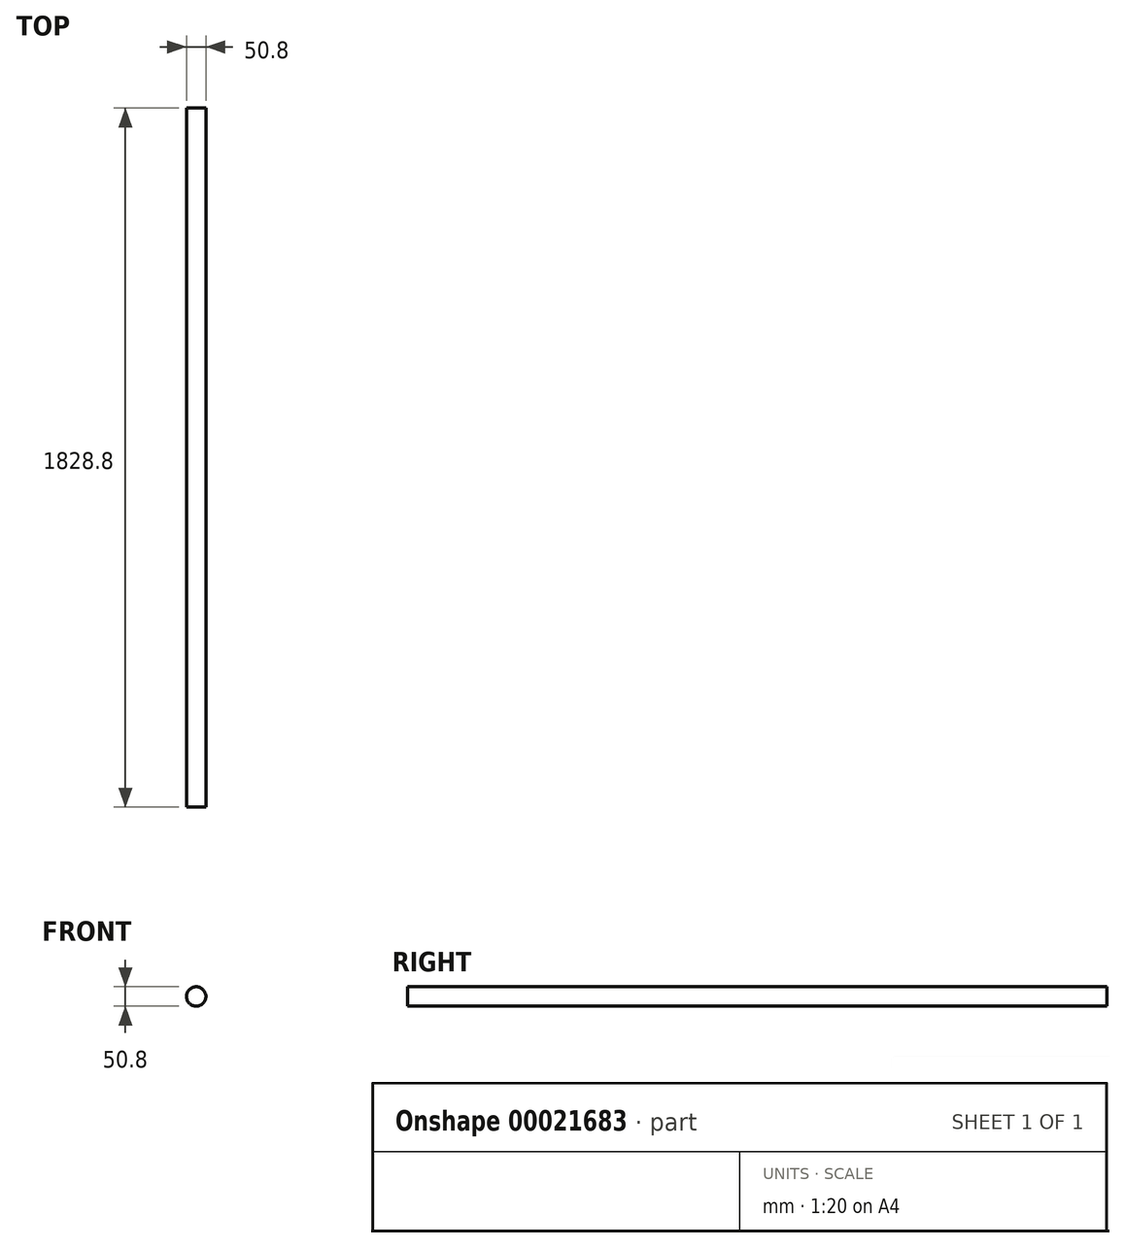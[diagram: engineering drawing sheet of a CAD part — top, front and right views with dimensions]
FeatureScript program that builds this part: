
annotation { "Feature Type Name" : "Feature", "Feature Type Description" : "" }
export const myFeature = defineFeature(function(context is Context, id is Id, definition is map)
    precondition{}
    {
        {
            var Q0;
            Q0=qCreatedBy(makeId("Front.planeOp"),FACE);
            var sketch = newSketch(context, id + "F0", { "sketchPlane" : qUnion([Q0])});
            skCircle(sketch, "E0", {"center": v(-43.74, 5.4) * mm, "radius": 25.4 * mm});
            skSolve(sketch);
        }
        {
            var Q0;
            Q0=makeQuery(id+"F0.imprint","IMPRINT",FACE,{"disambiguationData":[TD([[makeQuery(id+"F0.imprint","IMPRINT",EDGE,{"derivedFrom":sQuery(id+"F0.wireOp",EDGE,"E0")}),1.0]])]});
            extrude(context, id + "F1", {"entities" : qUnion([Q0]), "depth" : 1828.8 * mm});
        }
    });
